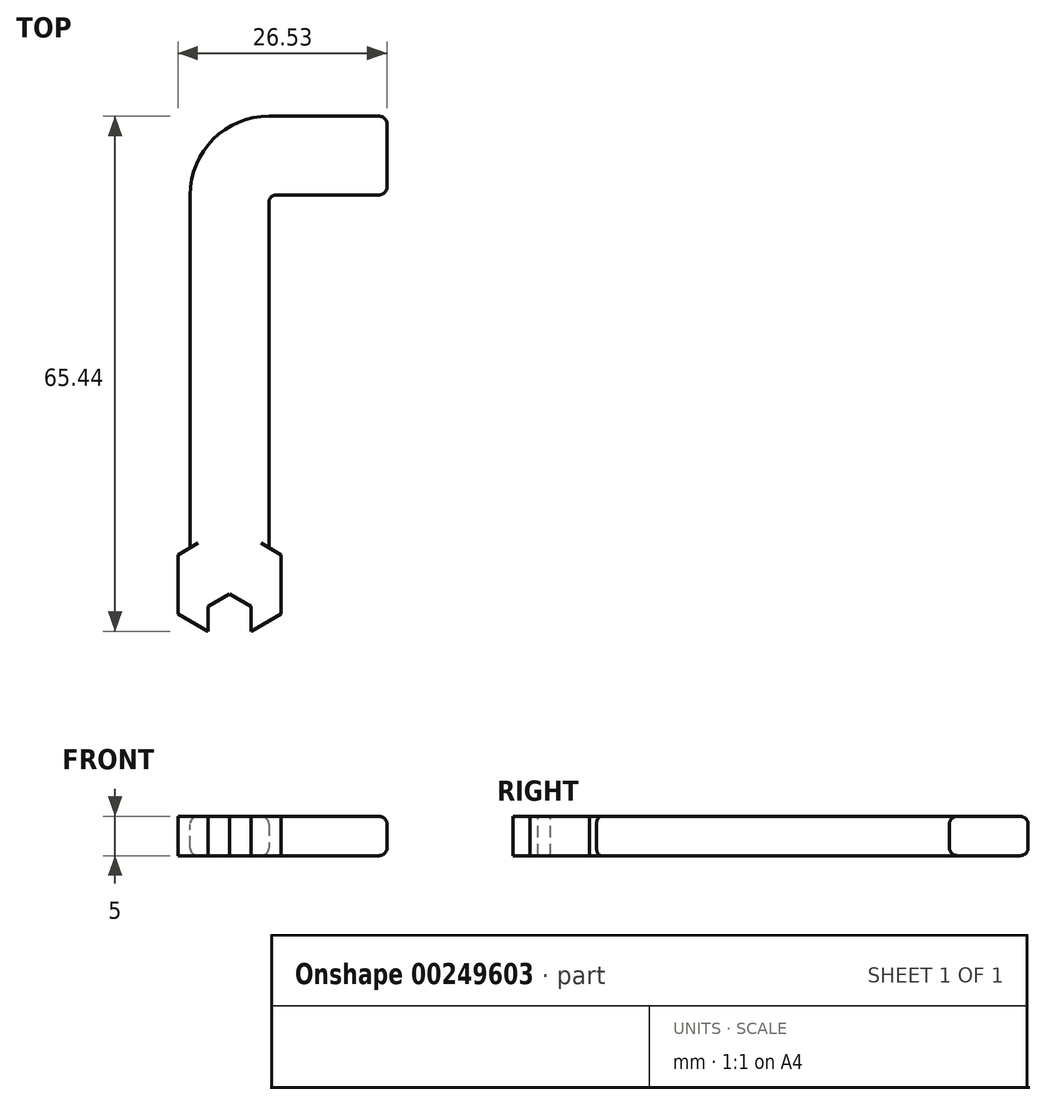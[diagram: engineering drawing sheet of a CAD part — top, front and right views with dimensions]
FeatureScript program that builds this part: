
annotation { "Feature Type Name" : "Feature", "Feature Type Description" : "" }
export const myFeature = defineFeature(function(context is Context, id is Id, definition is map)
    precondition{}
    {
        {
            var Q0;
            Q0=qCreatedBy(makeId("Front.planeOp"),FACE);
            var sketch = newSketch(context, id + "F0", { "sketchPlane" : qUnion([Q0])});
            skLineSegment(sketch, "E0.bottom", {"start": v(5, -2.5) * mm, "end": v(-5, -2.5) * mm});
            skLineSegment(sketch, "E0.top", {"start": v(5, 2.5) * mm, "end": v(-5, 2.5) * mm});
            skLineSegment(sketch, "E0.left", {"start": v(5, -2.5) * mm, "end": v(5, 2.5) * mm});
            skLineSegment(sketch, "E0.right", {"start": v(-5, -2.5) * mm, "end": v(-5, 2.5) * mm});
            skPoint(sketch, "E0.middle", {"position": v(0, 0) * mm});
            skSolve(sketch);
        }
        {
            var Q0;
            Q0=qCreatedBy(makeId("Top.planeOp"),FACE);
            var sketch = newSketch(context, id + "F1", { "sketchPlane" : qUnion([Q0])});
            skLineSegment(sketch, "E1", {"start": v(0, 0) * mm, "end": v(0, 45) * mm});
            skLineSegment(sketch, "E2", {"start": v(5, 50) * mm, "end": v(20, 50) * mm});
            skPoint(sketch, "E3.visualSharp", {"position": v(0, 50) * mm});
            skArc(sketch, "E3.filletArc", {"start": v(5, 50) * mm, "mid": v(1.46, 48.54) * mm, "end": v(0, 45) * mm});
            skSolve(sketch);
        }
        {
            var Q0;
            Q0=qSketchRegion(id+"F0",true);
            var Q1;
            Q1=qConstructionFilter(qBodyType(qCreatedBy(id+"F1",EDGE),BodyType.WIRE),ConstructionObject.NO);
            sweep(context, id + "F2", {"profiles" : qUnion([Q0]), "path" : qUnion([Q1])});
        }
        {
            var Q0;
            Q0=makeQuery(id+"F2.opSweep","SWEPT_FACE",FACE,{"disambiguationData":[OSD([sQuery(id+"F0.wireOp",EDGE,"E0.top"),sQuery(id+"F1.wireOp",EDGE,"E1")])]});
            var sketch = newSketch(context, id + "F3", { "sketchPlane" : qUnion([Q0])});
            skLineSegment(sketch, "E4.0", {"start": v(-5, 0) * mm, "end": v(5, 0) * mm});
            skLineSegment(sketch, "E4.3", {"start": v(5, -17.32) * mm, "end": v(-5, -17.32) * mm});
            skPoint(sketch, "E4.0.midPoint", {"position": v(0, 0) * mm});
            skCircle(sketch, "E5.cCircle", {"center": v(0, -4.48) * mm, "radius": 6.53 * mm, "construction": true});
            skLineSegment(sketch, "E5.0", {"start": v(6.53, -8.25) * mm, "end": v(0, -12.02) * mm});
            skLineSegment(sketch, "E5.1", {"start": v(0, -12.02) * mm, "end": v(-6.53, -8.25) * mm});
            skLineSegment(sketch, "E5.2", {"start": v(-6.53, -8.25) * mm, "end": v(-6.53, -0.7) * mm});
            skLineSegment(sketch, "E5.3", {"start": v(-6.53, -0.7) * mm, "end": v(0, 3.06) * mm});
            skLineSegment(sketch, "E5.4", {"start": v(0, 3.06) * mm, "end": v(6.53, -0.7) * mm});
            skLineSegment(sketch, "E5.5", {"start": v(6.53, -0.7) * mm, "end": v(6.53, -8.25) * mm});
            skPoint(sketch, "E5.0.midPoint", {"position": v(3.27, -10.14) * mm});
            skSolve(sketch);
        }
        {
            var Q0;
            Q0=qSketchRegion(id+"F3",true);
            var Q1;
            Q1=makeQuery(id+"F2.opSweep","SWEPT_FACE",FACE,{"disambiguationData":[OSD([sQuery(id+"F0.wireOp",EDGE,"E0.bottom"),sQuery(id+"F1.wireOp",EDGE,"E1")])]});
            extrude(context, id + "F4", {"entities" : qUnion([Q0]), "operationType" : NewBodyOperationType.ADD, "endBound" : BoundingType.UP_TO_SURFACE, "oppositeDirection" : true, "endBoundEntityFace" : qUnion([Q1]), "depth" : 25 * mm});
        }
        {
            var Q0;
            Q0=makeQuery(id+"F4.boolean.opBoolean","MERGE",FACE,{"derivedFrom":[makeQuery(id+"F2.opSweep","SWEPT_FACE",FACE,{"disambiguationData":[OSD([sQuery(id+"F0.wireOp",EDGE,"E0.top"),sQuery(id+"F1.wireOp",EDGE,"E1")])]}),makeQuery(id+"F4.opExtrude","CAP_FACE",FACE,{"disambiguationData":[OSD([sQuery(id+"F3.wireOp",EDGE,"E5.0"),sQuery(id+"F3.wireOp",EDGE,"E5.1"),sQuery(id+"F3.wireOp",EDGE,"E5.2"),sQuery(id+"F3.wireOp",EDGE,"E5.3"),sQuery(id+"F3.wireOp",EDGE,"E5.4"),sQuery(id+"F3.wireOp",EDGE,"E5.5")])],"isStart":true})]});
            var sketch = newSketch(context, id + "F5", { "sketchPlane" : qUnion([Q0])});
            skCircle(sketch, "E6.cCircle", {"center": v(0, -8.85) * mm, "radius": 2.75 * mm, "construction": true});
            skLineSegment(sketch, "E6.0", {"start": v(2.75, -10.44) * mm, "end": v(0, -12.02) * mm});
            skLineSegment(sketch, "E6.1", {"start": v(0, -12.02) * mm, "end": v(-2.75, -10.44) * mm});
            skLineSegment(sketch, "E6.2", {"start": v(-2.75, -10.44) * mm, "end": v(-2.75, -7.26) * mm});
            skLineSegment(sketch, "E6.3", {"start": v(-2.75, -7.26) * mm, "end": v(0, -5.67) * mm});
            skLineSegment(sketch, "E6.4", {"start": v(0, -5.67) * mm, "end": v(2.75, -7.26) * mm});
            skLineSegment(sketch, "E6.5", {"start": v(2.75, -7.26) * mm, "end": v(2.75, -10.44) * mm});
            skPoint(sketch, "E6.0.midPoint", {"position": v(1.37, -11.23) * mm});
            skSolve(sketch);
        }
        {
            var Q0;
            Q0=qSketchRegion(id+"F5",true);
            extrude(context, id + "F6", {"entities" : qUnion([Q0]), "operationType" : NewBodyOperationType.REMOVE, "endBound" : BoundingType.UP_TO_NEXT, "oppositeDirection" : true, "depth" : 25 * mm});
        }
        {
            var Q0;
            Q0=makeQuery(id+"F2.opSweep","CAP_EDGE",EDGE,{"disambiguationData":[OSD([sQuery(id+"F0.wireOp",EDGE,"E0.right"),sQuery(id+"F1.wireOp",VERTEX,"E2.end")])],"isStart":false});
            var Q1;
            Q1=makeQuery(id+"F2.opSweep","CAP_EDGE",EDGE,{"disambiguationData":[OSD([sQuery(id+"F0.wireOp",EDGE,"E0.left"),sQuery(id+"F1.wireOp",VERTEX,"E2.end")])],"isStart":false});
            var Q2;
            Q2=makeQuery(id+"F2.opSweep","MID_CAP_EDGE",EDGE,{"disambiguationData":[OSD([sQuery(id+"F0.wireOp",EDGE,"E0.left"),sQuery(id+"F1.wireOp",VERTEX,"E3.filletArc.start"),sQuery(id+"F1.wireOp",VERTEX,"E3.filletArc.end")])],"capPos":1.0});
            fillet(context, id + "F7", {"entities" : qUnion([Q0, Q1, Q2]), "radius" : 1 * mm, "tangentPropagation" : true, "allowEdgeOverflow" : false});
        }
        {
            var Q0;
            Q0=makeQuery(id+"F2.opSweep","CAP_EDGE",EDGE,{"disambiguationData":[OSD([sQuery(id+"F0.wireOp",EDGE,"E0.top"),sQuery(id+"F1.wireOp",VERTEX,"E2.end")])],"isStart":false});
            var Q1;
            Q1=makeQuery(id+"F2.opSweep","CAP_EDGE",EDGE,{"disambiguationData":[OSD([sQuery(id+"F0.wireOp",EDGE,"E0.bottom"),sQuery(id+"F1.wireOp",VERTEX,"E2.end")])],"isStart":false});
            fillet(context, id + "F8", {"entities" : qUnion([Q0, Q1]), "radius" : 1 * mm, "tangentPropagation" : true, "allowEdgeOverflow" : false});
        }
    });
